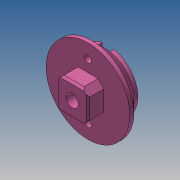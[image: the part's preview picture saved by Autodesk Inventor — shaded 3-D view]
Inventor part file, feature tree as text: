
AUTODESK INVENTOR PART (.ipt)
format: ipt  version: 2017 (Build 210142000, 142)  size: 237,568 bytes
history: native  units: mm
features: sketch x5, extrude x4, chamfer x2, other x1, revolve x1, hole x1, projected_geometry x1
ambient origin geometry x8: Origin, YZ Plane, XZ Plane, XY Plane, X Axis, Y Axis, Z Axis, Center Point
bodies: Body1 (feature_tree)
feature tree (15):
  other  "Sólido1"
  extrude  "Extrusión1"  Depth=11.85mm
  revolve  "Revolución1"  [1 undecoded]
  sketch  "Boceto2"  dims[d3=6.650287mm d4=3.7mm]
  extrude  "Extrusión2"  Depth=10.0mm
  extrude  "Extrusión3"  Depth=3.9mm
  extrude  "Extrusión4"  Depth=4.0mm TaperAngle=0.0deg
  chamfer  "Chaflán1"  Distance=8.0mm
  chamfer  "Chaflán3"  Distance=1.0mm Angle=45.0deg
  hole  "Agujero1"  [1 undecoded]
  sketch  "Boceto1"  dims[d0=6.3mm d2=11.85mm]
  projected_geometry  "Contorno proyectado1"
  sketch  "Boceto3"  dims[d5=10.0mm d6=0.0mm d7=4.2mm]
  sketch  "Boceto4"  dims[d8=120.0deg d9=3.9mm]
  sketch  "Boceto5"  dims[d10=30.0mm d11=0.0mm d12=4.0mm d13=0.0mm d14=8.0mm d15=0.0mm d23=1.0mm d24=2.0mm d25=45.0deg d26=30.0mm d27=4.075mm d28=4.075mm d32=16.0mm d33=55.0mm d36=1.0mm d37=2.0mm d38=45.0deg d39=3.0mm d40=3.0mm d41=3.0mm d42=3.0mm d43=3.0mm d44=3.0mm d45=3.0mm d46=3.0mm d47=45.0deg d48=21.0mm d49=2.0mm d50=90.0deg d51=28.0mm d52=3.575mm d53=6.0mm d54=6.5mm d55=3.0mm d56=90.0deg d57=8.0mm d58=20.594885mm]
note: 2 required parameter values undecoded (feature->parameter linkage not recoverable at this tier; creation-order binding heuristic only, values carry confidence <= 0.55)